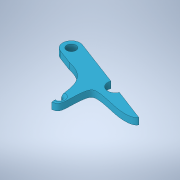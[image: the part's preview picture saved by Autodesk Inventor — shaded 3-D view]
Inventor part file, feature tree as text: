
AUTODESK INVENTOR PART (.ipt)
format: ipt  version: 2020.1 (Build 241239000, 239)  size: 171,008 bytes
history: native  units: mm
features: plane x2, sketch x2, extrude x1, fillet x1
ambient origin geometry x8: Origin, YZ Plane, XZ Plane, XY Plane, X Axis, Y Axis, Z Axis, Center Point
bodies: Solid1 (feature_tree)
feature tree (6):
  extrude  "Extrusion1"  Depth=26.3586mm
  fillet  "Fillet3"  Radius=4.0mm
  plane  "Work Plane1"
  plane  "Work Plane2"
  sketch  "Sketch3"  dims[d4=43.535mm d5=4.0mm d6=20.5358mm d7=7.0mm d9=1.5mm d10=1.2mm d13=3.0mm d14=0.0mm d21=17.3mm d22=2.6mm d23=20.507619mm d24=4.3mm d39=1.5mm d40=90.0deg]
  sketch  "Sketch1"  dims[d1=7.0mm d2=26.3586mm d3=4.0mm]
